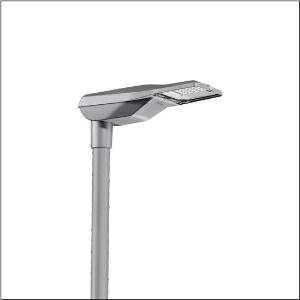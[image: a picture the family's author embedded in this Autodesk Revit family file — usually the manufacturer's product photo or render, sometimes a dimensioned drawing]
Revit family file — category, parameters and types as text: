
# Revit family: streetlight_sl_21_iq_micro___st0_8a_5xe1c41d08cb_e31f
name_source: partatom
category: Lighting Fixtures
units: mm (PartAtom-declared; Revit-internal decimal feet)

## family parameters
Cut with Voids When Loaded = No
Host = Face
Light Source = No
Part Type = Normal
Room Calculation Point = No
Round Connector Dimension = Use Diameter
Shared = No

## types (1)
- --- (1 x LED, 2980 lm, 19.4 W, 4000K)
    Apparent Load = 19 VA
    CIE Flux Codes = 38 75 97 100 100
    Color Rendering = 70
    Color Temperature = 4000K
    Default Elevation = 1800 mm
    Description = Streetlight SL 21 iQ micro, mast luminaire, primary light control with lens, of PMMA, primary optical cover: cover, of toughened safety glass, transparent, light distribution: ST0.8a, light emission: direct distribution, primary light characteristic: asymmetric, installation type: post-top, side-entry, LED, High Power LED, rated luminous flux: 2.980lm, luminous efficacy: 154lm/W, light colour: 740, colour temperature: 4000K, control: Auto-Match, Temp-Guard, Lumen-Switch, Night-Set, Smart-Wire, Light-Fading, Desk-Remote (wireless, voltage-free reading and setting of iQ features in the workshop via application-optimized NFC function/RFID function), optimised constant luminous flux control (CLO 2.0), presetting dimming linear, mains connection: 220..240V, AC, 50/60Hz, start of lifetime: 19W, end of service life: 20W, reduction: 10W, luminaire housing, of diecast aluminium, powder-coated, Siteco® metallic grey (DB 702S), corrosivity category C5 mid according to DIN EN ISO 12944, please order mast flange separately, inclination adjustable: 0°, 5°, 10°, 15°, sealing non-destructively replaceable, multi-level sealing system, length: 528mm, width: 235mm, height: 110mm, mast flange for spigot size: 42mm (side-entry): 5XC10008XM4, 60/48mm (side-entry/post-top): 5XC10108XM2, 76/60mm (side-entry/post-top): 5XC10108XM1, protection rating (complete): IP66, insulation class (complete): insulation class II (safety insulation), certification: CE, ENEC, ENEC+, VDE, impact resistance: IK09, permissible operating ambient temperature for outdoor applications: -40..+50°C, standard-compliant lighting for roads and squares, packaging unit: 1 piece

Light Distribution: ST0.8a
    Height = 110 mm
    Lamp = 1 x LED
    Lamp Light Flux = 2980 lm
    Lamp Power = 19.4 W
    Lamp count = 1
    Length = 528 mm
    Luminous efficacy = 154 lm/W
    Manufacturer = Siteco
    ModVariant = No
    Model = 5XE1C41D08CB
    Number of Poles = 1
    OnlyDefault = Yes
    Power Factor = 1
    Product Name = Streetlight SL 21 iQ micro | ST0.8a
    Product group = mast luminaire | pylon top
    ProductGroupID = 6100
    Protection Class = Protection class II
    Protection Degree = IP 66
    RLX_Detail_Level = 1
    RLX_Emergency_Light_Flux = 0 lm
    RLX_Emergency_Type = 0
    RLX_Emergency_Type_DB = No
    RlxData = <blob elided: 99061 chars, md5=b2a2ed5f>
    Socket = socket
    Standby Power = 0 W
    System Light Flux = 2980 lm
    System Power = 19 W
    Type Comments = factory setting: luminous flux: 100 % | dim-lin: 254 | 387 mA
    Type Image = l_1006881.jpg
    URL = http://relux.com
    VarID = @adj_069717
    Voltage = 0 V
    Weight = 0.00 kg
    Width = 235 mm

## geometry (parser evidence)
native form markers: Blend x4, Sweep x11
no freeform markers — native parametric forms only
